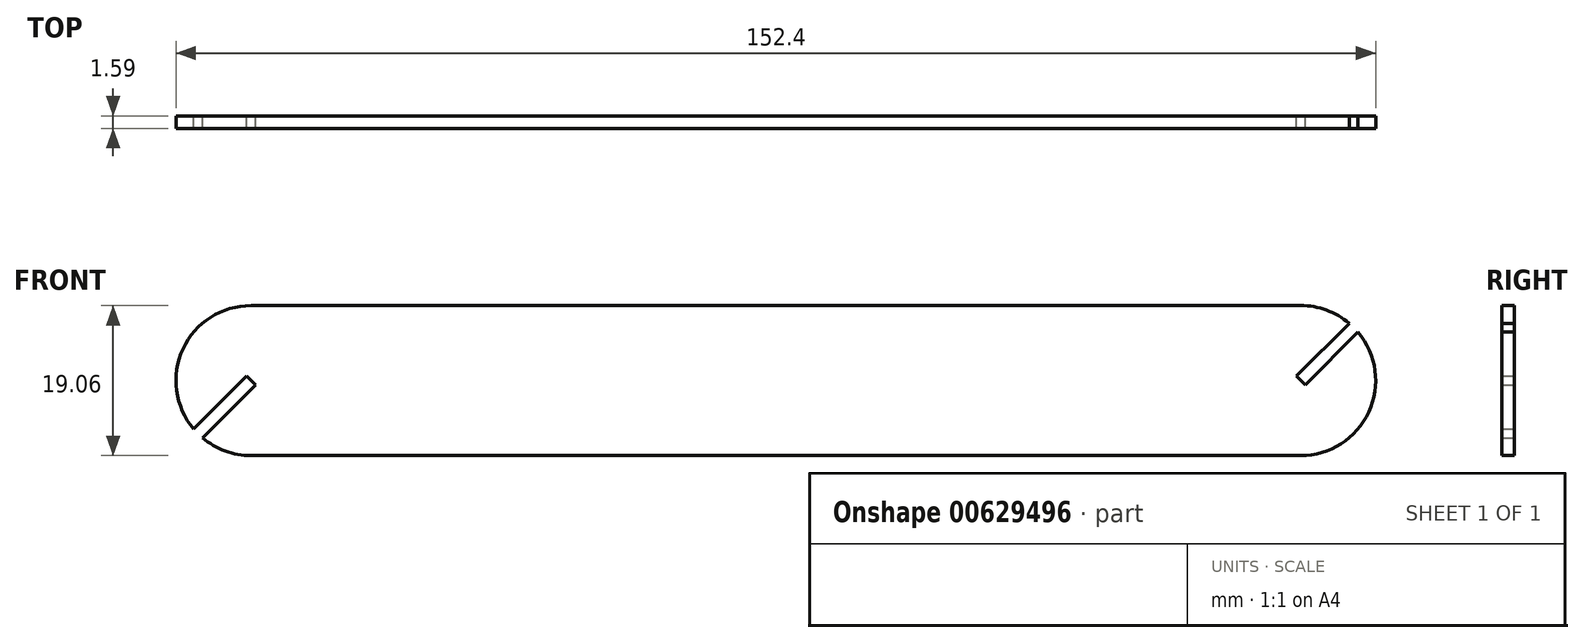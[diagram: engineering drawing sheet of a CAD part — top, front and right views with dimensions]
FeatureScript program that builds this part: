
annotation { "Feature Type Name" : "Feature", "Feature Type Description" : "" }
export const myFeature = defineFeature(function(context is Context, id is Id, definition is map)
    precondition{}
    {
        {
            var Q0;
            Q0=qCreatedBy(makeId("Front.planeOp"),FACE);
            var sketch = newSketch(context, id + "F0", { "sketchPlane" : qUnion([Q0])});
            skLineSegment(sketch, "E0.bottom", {"start": v(66.68, 9.53) * mm, "end": v(-66.68, 9.53) * mm});
            skLineSegment(sketch, "E0.top", {"start": v(66.68, -9.53) * mm, "end": v(-66.68, -9.53) * mm});
            skPoint(sketch, "E0.middle", {"position": v(0, 0) * mm});
            skArc(sketch, "E1", {"start": v(-66.68, 9.53) * mm, "mid": v(-76.2, 0) * mm, "end": v(-66.68, -9.53) * mm});
            skArc(sketch, "E2", {"start": v(66.68, -9.53) * mm, "mid": v(76.2, 0) * mm, "end": v(66.68, 9.53) * mm});
            skLineSegment(sketch, "E3", {"start": v(66.68, 0) * mm, "end": v(76.2, 0) * mm});
            skLineSegment(sketch, "E4", {"start": v(67.8, 0) * mm, "end": v(66.68, 0) * mm});
            skLineSegment(sketch, "E5", {"start": v(66.68, 0) * mm, "end": v(73.41, 6.74) * mm});
            skLineSegment(sketch, "E6", {"start": v(66.68, 0) * mm, "end": v(66.11, 0.56) * mm});
            skLineSegment(sketch, "E7", {"start": v(66.11, 0.56) * mm, "end": v(66.68, 0) * mm});
            skLineSegment(sketch, "E8", {"start": v(66.68, 0) * mm, "end": v(67.24, -0.56) * mm});
            skLineSegment(sketch, "E9", {"start": v(66.11, 0.56) * mm, "end": v(72.83, 7.27) * mm});
            skLineSegment(sketch, "E10", {"start": v(67.24, -0.56) * mm, "end": v(73.95, 6.15) * mm});
            skLineSegment(sketch, "E11", {"start": v(-66.68, 0) * mm, "end": v(-73.41, -6.74) * mm});
            skLineSegment(sketch, "E12", {"start": v(-66.68, 0) * mm, "end": v(-66.11, -0.56) * mm});
            skLineSegment(sketch, "E13", {"start": v(-66.68, 0) * mm, "end": v(-67.24, 0.56) * mm});
            skLineSegment(sketch, "E14", {"start": v(-66.11, -0.56) * mm, "end": v(-72.83, -7.27) * mm});
            skLineSegment(sketch, "E15", {"start": v(-67.24, 0.56) * mm, "end": v(-73.95, -6.15) * mm});
            skSolve(sketch);
        }
        {
            var Q0;
            {var subQ6=sQuery(id+"F0.wireOp",EDGE,"E0.bottom");Q0=makeQuery(id+"F0.imprint","IMPRINT",FACE,{"disambiguationData":[TD([[makeQuery(id+"F0.imprint","IMPRINT",EDGE,{"derivedFrom":subQ6}),1.0]])]});}
            var Q1;
            {var subQ0=sQuery(id+"F0.wireOp",EDGE,"E3");Q1=makeQuery(id+"F0.imprint","IMPRINT",FACE,{"disambiguationData":[TD([[makeQuery(id+"F0.imprint","IMPRINT",EDGE,{"derivedFrom":subQ0}),1.0]])]});}
            extrude(context, id + "F1", {"entities" : qUnion([Q0, Q1]), "depth" : 1.59 * mm, "offsetDistance" : 25.4 * mm});
        }
    });
